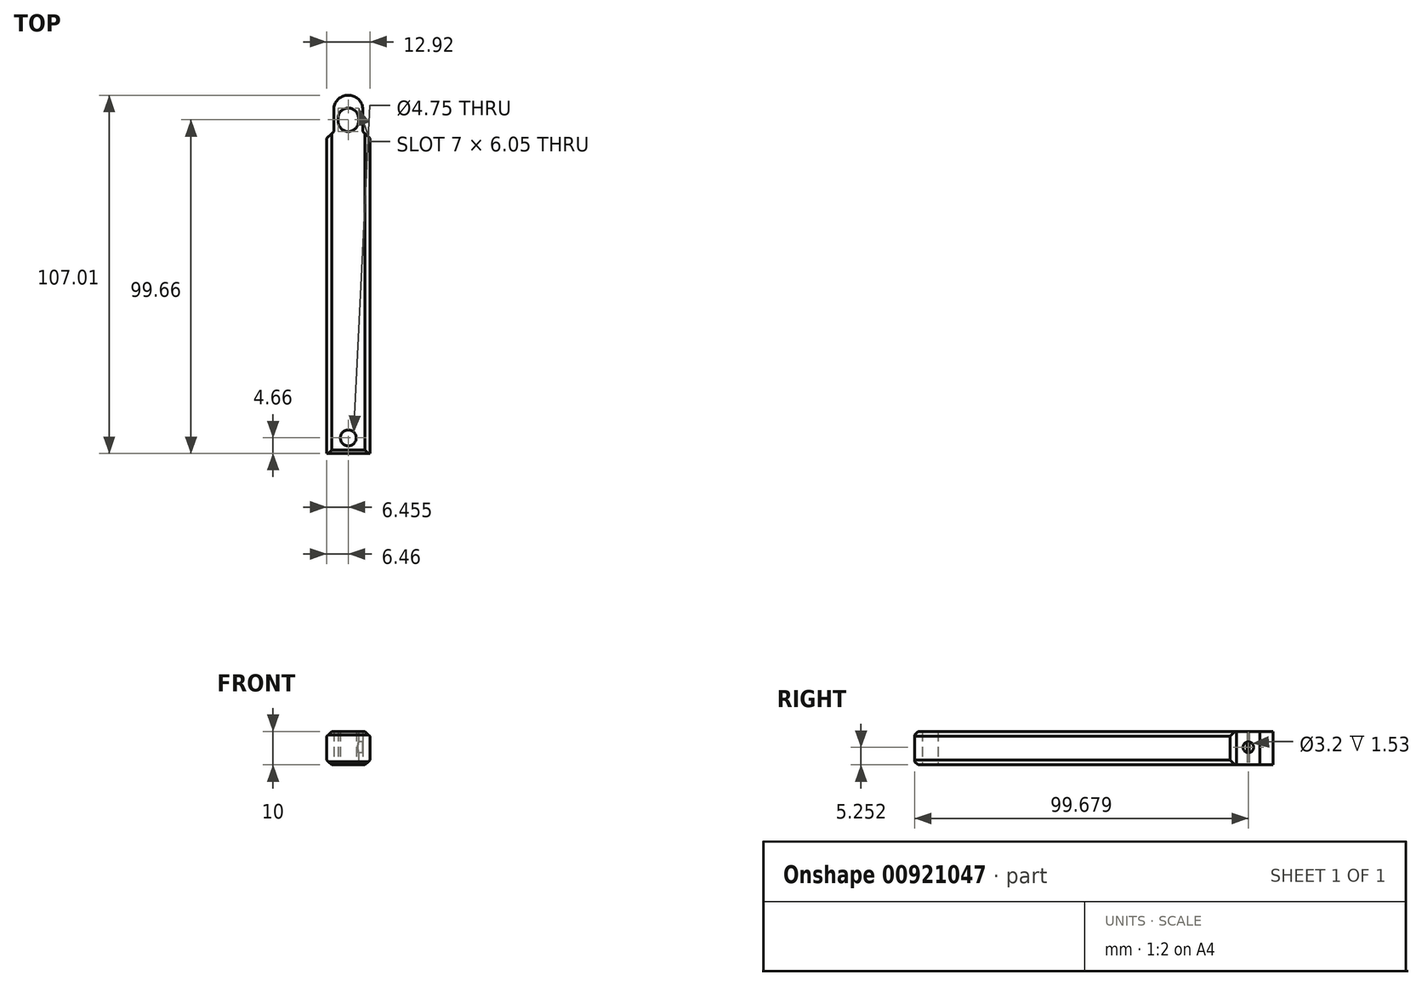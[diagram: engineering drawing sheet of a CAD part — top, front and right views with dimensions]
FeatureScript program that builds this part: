
annotation { "Feature Type Name" : "Feature", "Feature Type Description" : "" }
export const myFeature = defineFeature(function(context is Context, id is Id, definition is map)
    precondition{}
    {
        {
            var Q0;
            Q0=qCreatedBy(makeId("Top.planeOp"),FACE);
            var sketch = newSketch(context, id + "F0", { "sketchPlane" : qUnion([Q0])});
            skLineSegment(sketch, "E0", {"start": v(0, 0) * mm, "end": v(0, -47.5) * mm, "construction": true});
            skCircle(sketch, "E1", {"center": v(0, -47.5) * mm, "radius": 2.38 * mm});
            skLineSegment(sketch, "E2", {"start": v(0, 47.5) * mm, "end": v(-3, 47.5) * mm, "construction": true});
            skLineSegment(sketch, "E3", {"start": v(0, 47.5) * mm, "end": v(3, 47.5) * mm, "construction": true});
            skLineSegment(sketch, "E4", {"start": v(0, 47.5) * mm, "end": v(0, 51) * mm, "construction": true});
            skLineSegment(sketch, "E5", {"start": v(0, 47.5) * mm, "end": v(0, 44) * mm, "construction": true});
            skArc(sketch, "E6", {"start": v(3, 47.5) * mm, "mid": v(0, 51) * mm, "end": v(-3, 47.5) * mm});
            skArc(sketch, "E7", {"start": v(-3, 47.5) * mm, "mid": v(0, 44) * mm, "end": v(3, 47.5) * mm});
            skLineSegment(sketch, "E8", {"start": v(-3.03, 48.07) * mm, "end": v(-3.03, 46.88) * mm});
            skLineSegment(sketch, "E9", {"start": v(3.02, 46.75) * mm, "end": v(3.02, 48.25) * mm});
            skLineSegment(sketch, "E10", {"start": v(-4.33, 51) * mm, "end": v(-4.33, 44) * mm});
            skLineSegment(sketch, "E11.MirrorCS", {"start": v(4.33, 51) * mm, "end": v(4.33, 44) * mm});
            skArc(sketch, "E12", {"start": v(4.33, 51) * mm, "mid": v(0, 54.85) * mm, "end": v(-4.33, 51) * mm});
            skLineSegment(sketch, "E13", {"start": v(0, -52.16) * mm, "end": v(6.46, -52.16) * mm});
            skLineSegment(sketch, "E14", {"start": v(6.46, -52.16) * mm, "end": v(6.46, 42.02) * mm});
            skLineSegment(sketch, "E15", {"start": v(6.46, 42.02) * mm, "end": v(4.33, 44) * mm});
            skLineSegment(sketch, "E16.MirrorCS", {"start": v(-6.46, 42.02) * mm, "end": v(-4.33, 44) * mm});
            skLineSegment(sketch, "E17.MirrorCS", {"start": v(-6.46, -52.16) * mm, "end": v(-6.46, 42.02) * mm});
            skLineSegment(sketch, "E18.MirrorCS", {"start": v(0, -52.16) * mm, "end": v(-6.46, -52.16) * mm});
            skSolve(sketch);
        }
        {
            var Q0;
            Q0=makeQuery(id+"F0.imprint","IMPRINT",FACE,{"disambiguationData":[TD([[makeQuery(id+"F0.imprint","IMPRINT",EDGE,{"derivedFrom":sQuery(id+"F0.wireOp",EDGE,"E1")}),-1.0]])]});
            extrude(context, id + "F1", {"entities" : qUnion([Q0]), "depth" : 10 * mm, "offsetDistance" : 25.4 * mm});
        }
        {
            var Q0;
            Q0=qCreatedBy(makeId("Right.planeOp"),FACE);
            var sketch = newSketch(context, id + "F2", { "sketchPlane" : qUnion([Q0])});
            skLineSegment(sketch, "E19", {"start": v(44.02, 5.25) * mm, "end": v(51.02, 5.25) * mm, "construction": true});
            skLineSegment(sketch, "E20", {"start": v(47.53, 10.04) * mm, "end": v(47.53, 0) * mm, "construction": true});
            skCircle(sketch, "E21", {"center": v(47.52, 5.25) * mm, "radius": 1.6 * mm});
            skSolve(sketch);
        }
        {
            var Q0;
            Q0=makeQuery(id+"F2.imprint","IMPRINT",FACE,{"disambiguationData":[TD([[makeQuery(id+"F2.imprint","IMPRINT",EDGE,{"derivedFrom":sQuery(id+"F2.wireOp",EDGE,"E21")}),1.0]])]});
            extrude(context, id + "F3", {"entities" : qUnion([Q0]), "operationType" : NewBodyOperationType.REMOVE, "depth" : 25.4 * mm, "offsetDistance" : 25.4 * mm});
        }
        {
            var Q0;
            Q0=makeQuery(id+"F1.opExtrude","CAP_EDGE",EDGE,{"disambiguationData":[OSD([sQuery(id+"F0.wireOp",EDGE,"E14")])],"isStart":false});
            var Q1;
            Q1=makeQuery(id+"F1.opExtrude","CAP_EDGE",EDGE,{"disambiguationData":[OSD([sQuery(id+"F0.wireOp",EDGE,"E17.MirrorCS")])],"isStart":false});
            var Q2;
            Q2=makeQuery(id+"F1.opExtrude","CAP_EDGE",EDGE,{"disambiguationData":[OSD([sQuery(id+"F0.wireOp",EDGE,"E14")])],"isStart":true});
            var Q3;
            Q3=makeQuery(id+"F1.opExtrude","CAP_EDGE",EDGE,{"disambiguationData":[OSD([sQuery(id+"F0.wireOp",EDGE,"E17.MirrorCS")])],"isStart":true});
            chamfer(context, id + "F4", {"entities" : qUnion([Q0, Q1, Q2, Q3]), "width" : 1.5 * mm, "tangentPropagation" : true});
        }
        {
            var Q0;
            Q0=makeQuery(id+"F1.opExtrude","CAP_EDGE",EDGE,{"disambiguationData":[OSD([sQuery(id+"F0.wireOp",EDGE,"E13"),sQuery(id+"F0.wireOp",EDGE,"E18.MirrorCS")])],"isStart":true});
            var Q1;
            Q1=makeQuery(id+"F1.opExtrude","CAP_EDGE",EDGE,{"disambiguationData":[OSD([sQuery(id+"F0.wireOp",EDGE,"E13"),sQuery(id+"F0.wireOp",EDGE,"E18.MirrorCS")])],"isStart":false});
            chamfer(context, id + "F5", {"entities" : qUnion([Q0, Q1]), "width" : 1 * mm, "tangentPropagation" : true});
        }
    });
